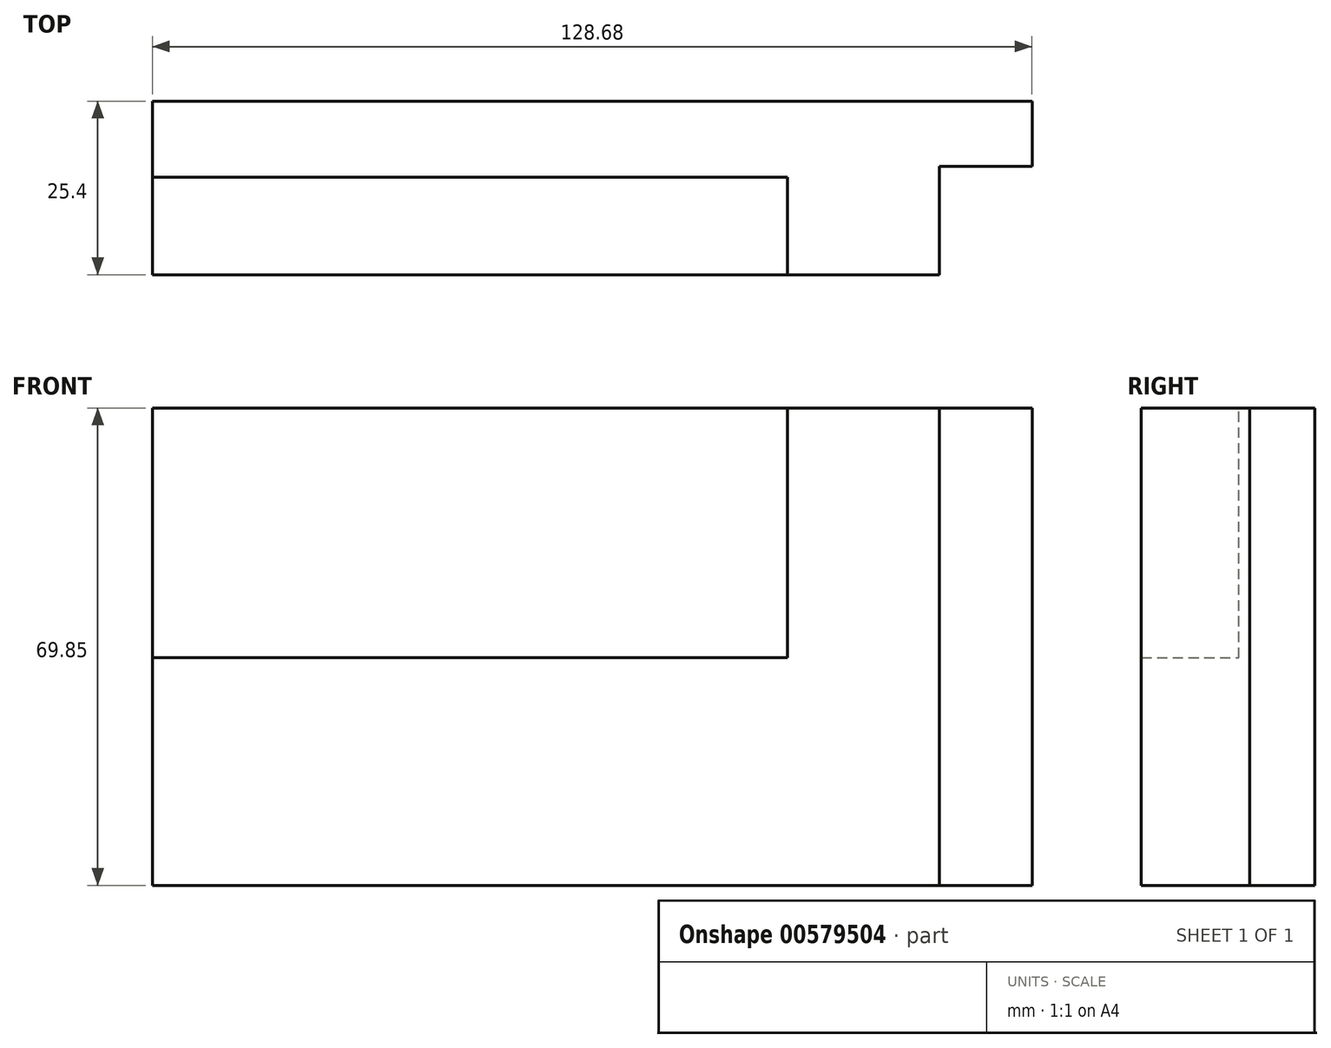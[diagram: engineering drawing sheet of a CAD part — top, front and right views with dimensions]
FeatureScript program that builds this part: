
annotation { "Feature Type Name" : "Feature", "Feature Type Description" : "" }
export const myFeature = defineFeature(function(context is Context, id is Id, definition is map)
    precondition{}
    {
        {
            var Q0;
            Q0=qCreatedBy(makeId("Front.planeOp"),FACE);
            var sketch = newSketch(context, id + "F0", { "sketchPlane" : qUnion([Q0])});
            skLineSegment(sketch, "E0", {"start": v(-64.9, 42.06) * mm, "end": v(-64.9, -27.8) * mm});
            skLineSegment(sketch, "E1", {"start": v(-64.9, 42.06) * mm, "end": v(63.78, 42.06) * mm});
            skLineSegment(sketch, "E2", {"start": v(63.78, 42.06) * mm, "end": v(63.78, -27.8) * mm});
            skLineSegment(sketch, "E3", {"start": v(-64.9, -27.8) * mm, "end": v(63.78, -27.8) * mm});
            skLineSegment(sketch, "E4", {"start": v(27.98, 5.5) * mm, "end": v(-64.9, 5.5) * mm});
            skPoint(sketch, "E5.end.orphan", {"position": v(45.76, -27.8) * mm});
            skLineSegment(sketch, "E6", {"start": v(50.2, 42.06) * mm, "end": v(50.2, -27.8) * mm});
            skLineSegment(sketch, "E7", {"start": v(27.98, 5.5) * mm, "end": v(27.98, 42.06) * mm});
            skSolve(sketch);
        }
        {
            var Q0;
            {var subQ0=sQuery(id+"F0.wireOp",EDGE,"E4");Q0=makeQuery(id+"F0.imprint","IMPRINT",FACE,{"disambiguationData":[TD([[makeQuery(id+"F0.imprint","IMPRINT",EDGE,{"derivedFrom":subQ0}),1.0]])]});}
            extrude(context, id + "F1", {"entities" : qUnion([Q0]), "depth" : 25.4 * mm, "offsetDistance" : 25.4 * mm});
        }
        {
            var Q0;
            {var subQ3=sQuery(id+"F0.wireOp",EDGE,"E4");Q0=makeQuery(id+"F0.imprint","IMPRINT",FACE,{"disambiguationData":[TD([[makeQuery(id+"F0.imprint","IMPRINT",EDGE,{"derivedFrom":subQ3}),-1.0]])]});}
            extrude(context, id + "F2", {"entities" : qUnion([Q0]), "operationType" : NewBodyOperationType.ADD, "depth" : 11.1 * mm, "offsetDistance" : 25.4 * mm});
        }
        {
            var Q0;
            {var subQ0=sQuery(id+"F0.wireOp",EDGE,"E2");Q0=makeQuery(id+"F0.imprint","IMPRINT",FACE,{"disambiguationData":[TD([[makeQuery(id+"F0.imprint","IMPRINT",EDGE,{"derivedFrom":subQ0}),-1.0]])]});}
            extrude(context, id + "F3", {"entities" : qUnion([Q0]), "operationType" : NewBodyOperationType.ADD, "depth" : 9.52 * mm, "offsetDistance" : 25.4 * mm});
        }
    });
